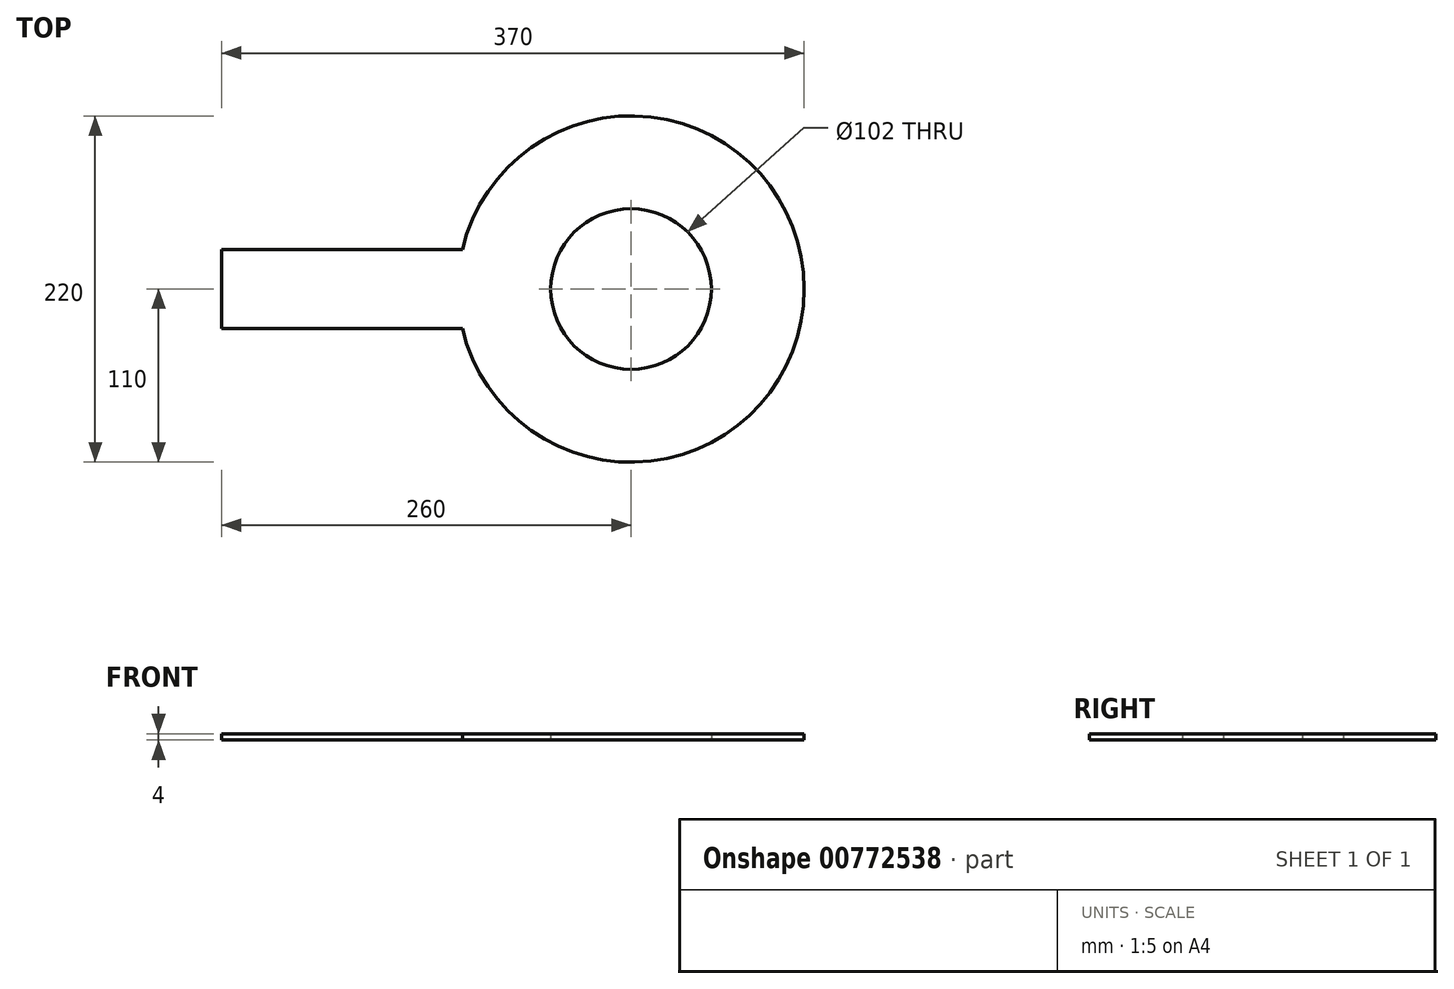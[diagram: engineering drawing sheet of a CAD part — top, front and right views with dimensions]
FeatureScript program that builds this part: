
annotation { "Feature Type Name" : "Feature", "Feature Type Description" : "" }
export const myFeature = defineFeature(function(context is Context, id is Id, definition is map)
    precondition{}
    {
        {
            var Q0;
            Q0=qCreatedBy(makeId("Top.planeOp"),FACE);
            var sketch = newSketch(context, id + "F0", { "sketchPlane" : qUnion([Q0])});
            skArc(sketch, "E0", {"start": v(-107.12, -25) * mm, "mid": v(110, 0) * mm, "end": v(-107.12, 25) * mm});
            skLineSegment(sketch, "E1.bottom", {"start": v(-107.12, 25) * mm, "end": v(-260, 25) * mm});
            skLineSegment(sketch, "E1.top", {"start": v(-107.12, -25) * mm, "end": v(-260, -25) * mm});
            skLineSegment(sketch, "E1.left", {"start": v(-110, 25) * mm, "end": v(-110, -25) * mm, "construction": true});
            skLineSegment(sketch, "E1.right", {"start": v(-260, 25) * mm, "end": v(-260, -25) * mm});
            skLineSegment(sketch, "E2", {"start": v(0, 0) * mm, "end": v(-110, 0) * mm, "construction": true});
            skCircle(sketch, "E3", {"center": v(0, 0) * mm, "radius": 51 * mm});
            skSolve(sketch);
        }
        {
            var Q0;
            Q0=makeQuery(id+"F0.imprint","IMPRINT",FACE,{"disambiguationData":[TD([[makeQuery(id+"F0.imprint","IMPRINT",EDGE,{"derivedFrom":sQuery(id+"F0.wireOp",EDGE,"E0")}),1.0]])]});
            extrude(context, id + "F1", {"entities" : qUnion([Q0]), "depth" : 4 * mm, "offsetDistance" : 25 * mm});
        }
    });
